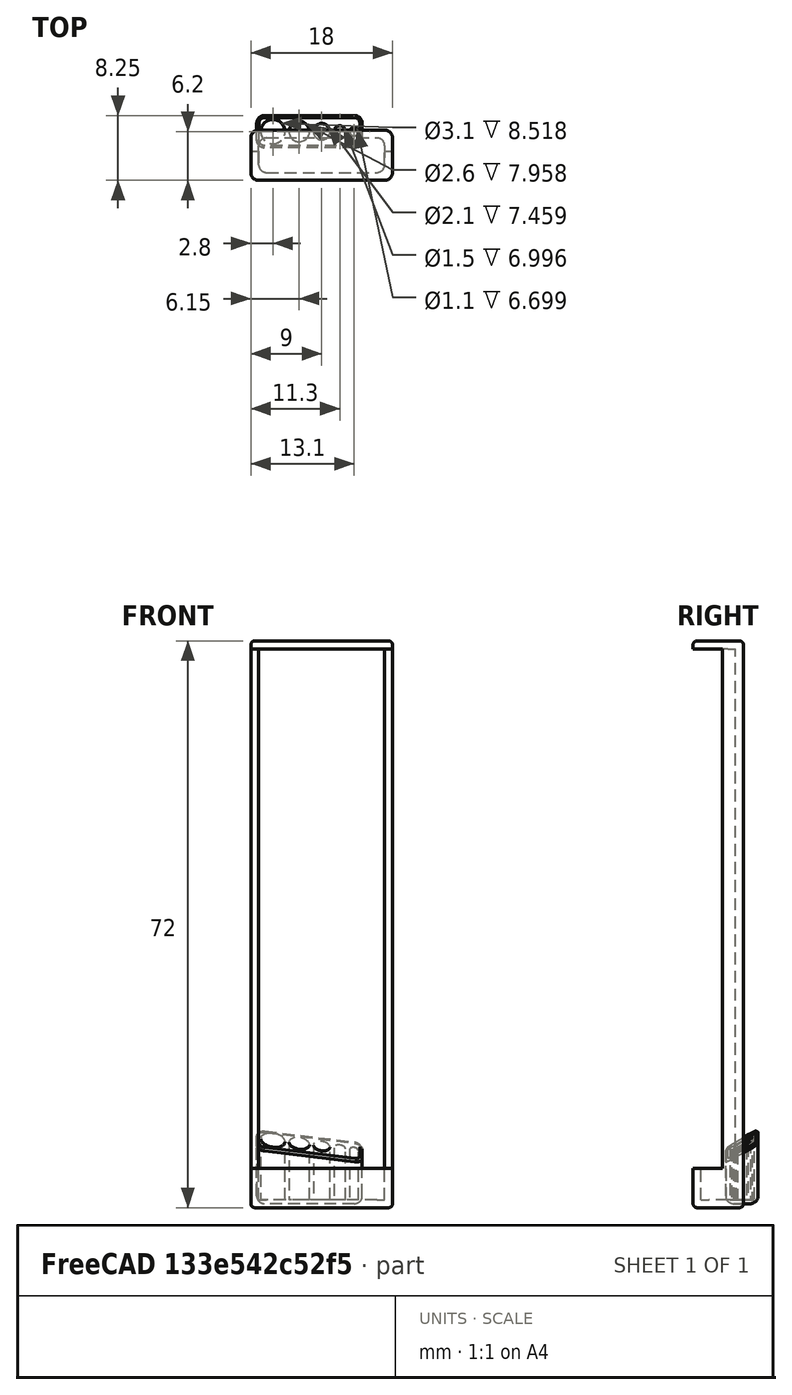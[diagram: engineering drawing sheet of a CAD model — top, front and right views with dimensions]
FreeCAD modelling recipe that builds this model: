
FCSTD DOCUMENT  (FreeCAD 0.20R29177 (Git))
Label: tiny_drillbit_holder
License: All rights reserved
LicenseURL: http://en.wikipedia.org/wiki/All_rights_reserved
objects: PartDesign::Pad×5, TechDraw::DrawViewDimension×5, Sketcher::SketchObject×4, PartDesign::Fillet×3, TechDraw::DrawProjGroupItem×3, PartDesign::ShapeBinder×2, PartDesign::Draft×2, PartDesign::Body×2, PartDesign::Chamfer×1, TechDraw::DrawSVGTemplate×1, TechDraw::DrawProjGroup×1, TechDraw::DrawPage×1, PartDesign::Pocket×1, PartDesign::Plane×1
note: 33 computed .brp shape members not serialized (recipe doc carries the construction recipe); baked Part::Feature solids carry a one-line shape summary decoded from their .brp

FEATURE [Sketcher::SketchObject] Sketch
  Base_Annotations = Drill Hole sizes (all mm) | 1 | 1.5 | 2 | 2.5 | 3
  FullyConstrained = true
  MapMode = 5
  Support = -> [XY_Plane]
  sketch-geometry (22):
    g0: LineSegment StartX=-8.25 StartY=2.05 StartZ=0 EndX=5.15 EndY=2.05 EndZ=0
    g1: LineSegment StartX=5.15 StartY=2.05 StartZ=0 EndX=5.15 EndY=-2.05 EndZ=0
    g2: LineSegment StartX=5.15 StartY=-2.05 StartZ=0 EndX=-8.25 EndY=-2.05 EndZ=0
    g3: LineSegment StartX=-8.25 StartY=-2.05 StartZ=0 EndX=-8.25 EndY=2.05 EndZ=0
    g4: Circle CenterX=-6.2 CenterY=0 CenterZ=0 NormalX=0 NormalY=0 NormalZ=1 AngleXU=0 Radius=1.55
    g5: Circle CenterX=-2.85 CenterY=0 CenterZ=0 NormalX=0 NormalY=0 NormalZ=1 AngleXU=0 Radius=1.3
    g6: Circle CenterX=0 CenterY=0 CenterZ=0 NormalX=0 NormalY=0 NormalZ=1 AngleXU=0 Radius=1.05
    g7: Circle CenterX=2.3 CenterY=0 CenterZ=0 NormalX=0 NormalY=0 NormalZ=1 AngleXU=0 Radius=0.75
    g8: Circle CenterX=4.1 CenterY=0 CenterZ=0 NormalX=0 NormalY=0 NormalZ=1 AngleXU=0 Radius=0.55
    g9: GeomPoint X=-4.15 Y=0 Z=0
    g10: GeomPoint X=-4.65 Y=0 Z=0
    g11: GeomPoint X=-1.55 Y=0 Z=0
    g12: GeomPoint X=-1.05 Y=0 Z=0
    g13: GeomPoint X=1.05 Y=0 Z=0
    g14: GeomPoint X=1.55 Y=0 Z=0
    g15: GeomPoint X=3.05 Y=0 Z=0
    g16: GeomPoint X=3.55 Y=0 Z=0
    g17: GeomPoint X=4.65 Y=0 Z=0
    g18: GeomPoint X=5.15 Y=0 Z=0
    g19: GeomPoint X=-7.75 Y=0 Z=0
    g20: GeomPoint X=-8.25 Y=0 Z=0
    g21: GeomPoint X=-6.2 Y=1.55 Z=0
  constraints (51):
    c: Coincident(g0,g1)
    c: Coincident(g1,g2)
    c: Coincident(g2,g3)
    c: Coincident(g3,g0)
    c: Horizontal(g0)
    c: Horizontal(g2)
    c: Vertical(g1)
    c: PointOnObject(g4,g-1)
    c: Diameter(g4) = 3.1
    c: PointOnObject(g5,g-1)
    c: PointOnObject(g7,g-1)
    c: PointOnObject(g8,g-1)
    c: Diameter(g8) = 1.1
    c: Diameter(g7) = 1.5
    c: Diameter(g6) = 2.1
    c: Diameter(g5) = 2.6
    c: Coincident(g6,g-1)
    c: PointOnObject(g9,g5)
    c: PointOnObject(g10,g4)
    c: PointOnObject(g11,g5)
    c: PointOnObject(g12,g6)
    c: PointOnObject(g13,g6)
    c: PointOnObject(g14,g7)
    c: PointOnObject(g15,g7)
    c: PointOnObject(g16,g8)
    c: PointOnObject(g17,g8)
    c: PointOnObject(g18,g1)
    c: PointOnObject(g19,g4)
    c: PointOnObject(g20,g3)
    c: PointOnObject(g17,g-1)
    c: PointOnObject(g16,g-1)
    c: PointOnObject(g15,g-1)
    c: PointOnObject(g14,g-1)
    c: PointOnObject(g13,g-1)
    c: PointOnObject(g11,g-1)
    c: PointOnObject(g9,g-1)
    c: PointOnObject(g10,g-1)
    c: PointOnObject(g19,g-1)
    c: PointOnObject(g20,g-1)
    c: PointOnObject(g18,g-1)
    c: DistanceX(g15,g16) = 0.5
    c: DistanceX(g13,g14) = 0.5
    c: PointOnObject(g12,g-1)
    c: DistanceX(g11,g12) = 0.5
    c: DistanceX(g20,g19) = 0.5
    c: DistanceX(g10,g9) = 0.5
    c: DistanceX(g17,g18) = 0.5
    c: PointOnObject(g21,g4)
    c: Vertical(g21,g4)
    c: DistanceY(g21,g0) = 0.5
    c: Symmetric(g0,g2,g-1)
FEATURE [PartDesign::ShapeBinder] ShapeBinder
  Support = -> [Sketch]
  TraceSupport = false
FEATURE [PartDesign::Pad] Pad
  Direction = (0,0,1)
  Length = 0.5
  Length2 = 10
  Profile = -> ShapeBinder
  Reversed = true
  Type = 0
FEATURE [PartDesign::Pad] Pad001
  BaseFeature = -> Pad
  Direction = (0,0,1)
  Length = 9
  Length2 = 10
  Profile = -> Sketch
  ReferenceAxis = -> Sketch [N_Axis]
  Type = 0
FEATURE [PartDesign::Draft] Draft
  Angle = 30
  Base = -> Pad001 [Face9]
  BaseFeature = -> Pad001
  SupportTransform = false
FEATURE [PartDesign::Draft] Draft001
  Angle = 6
  Base = -> Draft [Face9]
  BaseFeature = -> Draft
  NeutralPlane = -> Draft [Face8]
  Reversed = true
  SupportTransform = false
FEATURE [PartDesign::Fillet] Fillet
  Base = -> Draft001 [Edge11,Edge1,Edge7,Edge16,Edge5,Edge14,Edge18,Edge8,Edge10,Edge2,Edge12,Edge4]
  BaseFeature = -> Draft001
  Radius = 1
  SupportTransform = false
  UseAllEdges = false
FEATURE [PartDesign::Chamfer] Chamfer
  Angle = 45
  Base = -> Fillet [Edge8,Edge6,Edge5,Edge7,Edge9,Edge11,Edge1,Edge10]
  BaseFeature = -> Fillet
  ChamferType = 0
  FlipDirection = false
  Size = 0.3
  Size2 = 1
  SupportTransform = false
  UseAllEdges = false
FEATURE [PartDesign::Body] Body
  Group = -> [Sketch,ShapeBinder,Pad,Pad001,Draft,Draft001,Fillet,Chamfer]
  Origin = -> Origin
  Placement = pos=(0,3,0) rot=(0,0,1;0rad)
  Tip = -> Chamfer
FEATURE [TechDraw::DrawSVGTemplate] Template
  Height = 210
  Orientation = 1
  Width = 297
FEATURE [TechDraw::DrawProjGroupItem] ProjItem  label="Front"
  CoarseView = false
  Direction = (0,0,-1)
  Focus = 100
  HardHidden = false
  IsoCount = 0
  IsoHidden = false
  IsoVisible = false
  LockPosition = true
  Perspective = false
  Rotation = 0
  RotationVector = (1,0,0)
  Scale = 4
  ScaleType = 2
  SeamHidden = false
  SeamVisible = true
  SmoothHidden = false
  SmoothVisible = true
  Source = -> [Body]
  Type = 0
  X = 0
  XDirection = (1,0,0)
  Y = 0
FEATURE [TechDraw::DrawProjGroupItem] ProjItem001  label="Left"
  CoarseView = false
  Direction = (-1,0,-1e-16)
  Focus = 100
  HardHidden = false
  IsoCount = 0
  IsoHidden = false
  IsoVisible = false
  LockPosition = false
  Perspective = false
  Rotation = 0
  RotationVector = (1,0,0)
  Scale = 4
  ScaleType = 2
  SeamHidden = false
  SeamVisible = true
  SmoothHidden = false
  SmoothVisible = true
  Source = -> [Body]
  Type = 1
  X = 60.2775
  XDirection = (1e-16,0,-1)
  Y = 0
FEATURE [TechDraw::DrawProjGroupItem] ProjItem002  label="Top"
  CoarseView = false
  Direction = (0,-1,0)
  Focus = 100
  HardHidden = false
  IsoCount = 0
  IsoHidden = false
  IsoVisible = false
  LockPosition = false
  Perspective = false
  Rotation = 0
  RotationVector = (1,0,0)
  Scale = 4
  ScaleType = 2
  SeamHidden = false
  SeamVisible = true
  SmoothHidden = false
  SmoothVisible = true
  Source = -> [Body]
  Type = 4
  X = 0
  XDirection = (1,0,0)
  Y = -51.9549
FEATURE [TechDraw::DrawProjGroup] ProjGroup
  Anchor = -> ProjItem
  AutoDistribute = true
  LockPosition = false
  ProjectionType = 0
  Rotation = 0
  Scale = 4
  ScaleType = 2
  Source = -> [Body]
  Views = -> [ProjItem,ProjItem001,ProjItem002]
  X = 117.659
  Y = 133.282
  spacingX = 15
  spacingY = 15
FEATURE [TechDraw::DrawViewDimension] Dimension
  AngleOverride = false
  Arbitrary = false
  ArbitraryTolerances = false
  EqualTolerance = true
  ExtensionAngle = 0
  FormatSpec = %.2f
  FormatSpecOverTolerance = %+.2f
  FormatSpecUnderTolerance = %+.2f
  Inverted = false
  LineAngle = 0
  LockPosition = false
  MeasureType = 1
  OverTolerance = 0
  References2D = -> [ProjItem]
  Rotation = 0
  ScaleType = 0
  TheoreticalExact = false
  Type = 1
  UnderTolerance = 0
  X = 0.767824
  Y = 30.3865
FEATURE [TechDraw::DrawViewDimension] Dimension001
  AngleOverride = false
  Arbitrary = false
  ArbitraryTolerances = false
  EqualTolerance = true
  ExtensionAngle = 0
  FormatSpec = %.2f
  FormatSpecOverTolerance = %+.2f
  FormatSpecUnderTolerance = %+.2f
  Inverted = false
  LineAngle = 0
  LockPosition = false
  MeasureType = 1
  OverTolerance = 0
  References2D = -> [ProjItem]
  Rotation = 0
  ScaleType = 0
  TheoreticalExact = false
  Type = 2
  UnderTolerance = 0
  X = -51.8494
  Y = 2.12797
FEATURE [TechDraw::DrawViewDimension] Dimension002
  AngleOverride = false
  Arbitrary = false
  ArbitraryTolerances = false
  EqualTolerance = true
  ExtensionAngle = 0
  FormatSpec = R%.2f
  FormatSpecOverTolerance = %+.2f
  FormatSpecUnderTolerance = %+.2f
  Inverted = false
  LineAngle = 0
  LockPosition = false
  MeasureType = 1
  OverTolerance = 0
  References2D = -> [ProjItem]
  Rotation = 0
  ScaleType = 0
  TheoreticalExact = false
  Type = 4
  UnderTolerance = 0
  X = -32.5046
  Y = 16.7642
FEATURE [TechDraw::DrawViewDimension] Dimension003
  AngleOverride = false
  Arbitrary = false
  ArbitraryTolerances = false
  EqualTolerance = true
  ExtensionAngle = 0
  FormatSpec = %.2f
  FormatSpecOverTolerance = %+.2f
  FormatSpecUnderTolerance = %+.2f
  Inverted = false
  LineAngle = 0
  LockPosition = false
  MeasureType = 1
  OverTolerance = 0
  References2D = -> [ProjItem002]
  Rotation = 0
  ScaleType = 0
  TheoreticalExact = false
  Type = 2
  UnderTolerance = 0
  X = 37.6446
  Y = -1.60291
FEATURE [TechDraw::DrawViewDimension] Dimension004
  AngleOverride = false
  Arbitrary = false
  ArbitraryTolerances = false
  EqualTolerance = true
  ExtensionAngle = 0
  FormatSpec = R%.2f
  FormatSpecOverTolerance = %+.2f
  FormatSpecUnderTolerance = %+.2f
  Inverted = false
  LineAngle = 0
  LockPosition = false
  MeasureType = 1
  OverTolerance = 0
  References2D = -> [ProjItem002]
  Rotation = 0
  ScaleType = 0
  TheoreticalExact = false
  Type = 4
  UnderTolerance = 0
  X = -34.2962
  Y = -22.1389
FEATURE [TechDraw::DrawPage] Page
  KeepUpdated = true
  NextBalloonIndex = 1
  ProjectionType = 0
  Template = -> Template
  Views = -> [ProjGroup,Dimension,Dimension001,Dimension002,Dimension003,Dimension004]
FEATURE [Sketcher::SketchObject] Sketch001
  FullyConstrained = true
  MapMode = 5
  Support = -> [XY_Plane001]
  sketch-geometry (20):
    g0: ArcOfCircle CenterX=-7 CenterY=1.2 CenterZ=0 NormalX=0 NormalY=0 NormalZ=1 AngleXU=0 Radius=1 StartAngle=1.5708 EndAngle=3.14159
    g1: LineSegment StartX=-7 StartY=2.2 StartZ=0 EndX=7 EndY=2.2 EndZ=0
    g2: ArcOfCircle CenterX=7 CenterY=1.2 CenterZ=0 NormalX=0 NormalY=0 NormalZ=1 AngleXU=0 Radius=1 StartAngle=1e-16 EndAngle=1.5708
    g3: LineSegment StartX=8 StartY=1.2 StartZ=0 EndX=8 EndY=-1.2 EndZ=0
    g4: ArcOfCircle CenterX=7 CenterY=-1.2 CenterZ=0 NormalX=0 NormalY=0 NormalZ=1 AngleXU=0 Radius=1 StartAngle=4.71239 EndAngle=6.28319
    g5: LineSegment StartX=7 StartY=-2.2 StartZ=0 EndX=-7 EndY=-2.2 EndZ=0
    g6: ArcOfCircle CenterX=-7 CenterY=-1.2 CenterZ=0 NormalX=0 NormalY=0 NormalZ=1 AngleXU=0 Radius=1 StartAngle=3.14159 EndAngle=4.71239
    g7: LineSegment StartX=-8 StartY=-1.2 StartZ=0 EndX=-8 EndY=1.2 EndZ=0
    g8: GeomPoint X=-8 Y=2.2 Z=0
    g9: GeomPoint X=8 Y=-2.2 Z=0
    g10: ArcOfCircle CenterX=-8 CenterY=2.2 CenterZ=0 NormalX=0 NormalY=0 NormalZ=1 AngleXU=0 Radius=1 StartAngle=1.5708 EndAngle=3.14159
    g11: LineSegment StartX=-8 StartY=3.2 StartZ=0 EndX=8 EndY=3.2 EndZ=0
    g12: ArcOfCircle CenterX=8 CenterY=2.2 CenterZ=0 NormalX=0 NormalY=0 NormalZ=1 AngleXU=0 Radius=1 StartAngle=2e-16 EndAngle=1.5708
    g13: LineSegment StartX=9 StartY=2.2 StartZ=0 EndX=9 EndY=-2.2 EndZ=0
    g14: ArcOfCircle CenterX=8 CenterY=-2.2 CenterZ=0 NormalX=0 NormalY=0 NormalZ=1 AngleXU=0 Radius=1 StartAngle=4.71239 EndAngle=6.28319
    g15: LineSegment StartX=8 StartY=-3.2 StartZ=0 EndX=-8 EndY=-3.2 EndZ=0
    g16: ArcOfCircle CenterX=-8 CenterY=-2.2 CenterZ=0 NormalX=0 NormalY=0 NormalZ=1 AngleXU=0 Radius=1 StartAngle=3.14159 EndAngle=4.71239
    g17: LineSegment StartX=-9 StartY=-2.2 StartZ=0 EndX=-9 EndY=2.2 EndZ=0
    g18: GeomPoint X=-9 Y=3.2 Z=0
    g19: GeomPoint X=9 Y=-3.2 Z=0
  constraints (46):
    c: Tangent(g0,g1) = 1.5708
    c: Tangent(g1,g2) = 1.5708
    c: Tangent(g2,g3) = 1.5708
    c: Tangent(g3,g4) = 1.5708
    c: Tangent(g4,g5) = 1.5708
    c: Tangent(g5,g6) = 1.5708
    c: Tangent(g6,g7) = 1.5708
    c: Tangent(g7,g0) = 1.5708
    c: Horizontal(g1)
    c: Horizontal(g5)
    c: Vertical(g3)
    c: Vertical(g7)
    c: Equal(g0,g2)
    c: Equal(g2,g4)
    c: Equal(g4,g6)
    c: PointOnObject(g8,g1)
    c: PointOnObject(g8,g7)
    c: PointOnObject(g9,g3)
    c: PointOnObject(g9,g5)
    c: Tangent(g10,g11) = 1.5708
    c: Tangent(g11,g12) = 1.5708
    c: Tangent(g12,g13) = 1.5708
    c: Tangent(g13,g14) = 1.5708
    c: Tangent(g14,g15) = 1.5708
    c: Tangent(g15,g16) = 1.5708
    c: Tangent(g16,g17) = 1.5708
    c: Tangent(g17,g10) = 1.5708
    c: Horizontal(g11)
    c: Horizontal(g15)
    c: Vertical(g13)
    c: Vertical(g17)
    c: Equal(g10,g12)
    c: Equal(g12,g14)
    c: Equal(g14,g16)
    c: PointOnObject(g18,g11)
    c: PointOnObject(g18,g17)
    c: PointOnObject(g19,g13)
    c: PointOnObject(g19,g15)
    c: Symmetric(g4,g0,g-1)
    c: Symmetric(g14,g10,g-1)
    c: DistanceX(g10,g0) = 1
    c: DistanceY(g0,g10) = 1
    c: Radius(g6) = 1
    c: DistanceY(g4,g1) = 4.4
    c: DistanceX(g5,g5) = 14
    c: Equal(g16,g6)
FEATURE [PartDesign::ShapeBinder] ShapeBinder001
  Support = -> [Sketch001]
  TraceSupport = false
FEATURE [PartDesign::Pad] Pad002
  Direction = (0,0,1)
  Length = 1
  Length2 = 10
  Profile = -> ShapeBinder001
  Reversed = true
  Type = 0
FEATURE [PartDesign::Pad] Pad003
  BaseFeature = -> Pad002
  Direction = (0,0,1)
  Length = 70
  Length2 = 10
  Profile = -> Sketch001
  ReferenceAxis = -> Sketch001 [N_Axis]
  Type = 0
FEATURE [Sketcher::SketchObject] Sketch002
  ExternalGeometry = -> [Sketch001]
  FullyConstrained = true
  MapMode = 5
  Placement = pos=(0,0,0) rot=(1,0,0;1.5708rad)
  Support = -> [XZ_Plane001]
  sketch-geometry (4):
    g0: LineSegment StartX=-9 StartY=4 StartZ=0 EndX=9 EndY=4 EndZ=0
    g1: LineSegment StartX=9 StartY=4 StartZ=0 EndX=9 EndY=70 EndZ=0
    g2: LineSegment StartX=9 StartY=70 StartZ=0 EndX=-9 EndY=70 EndZ=0
    g3: LineSegment StartX=-9 StartY=70 StartZ=0 EndX=-9 EndY=4 EndZ=0
  constraints (11):
    c: Coincident(g0,g1)
    c: Coincident(g1,g2)
    c: Coincident(g2,g3)
    c: Coincident(g3,g0)
    c: Horizontal(g2)
    c: Vertical(g1)
    c: Vertical(g3)
    c: Symmetric(g0,g0,g-2)
    c: Vertical(g0,g-3)
    c: DistanceY(g-3,g0) = 4
    c: DistanceY(g-3,g2) = 70
FEATURE [PartDesign::Pocket] Pocket
  BaseFeature = -> Pad003
  Direction = (0,1,-2e-16)
  Length = 5
  Length2 = 0.5
  Profile = -> Sketch002
  ReferenceAxis = -> Sketch002 [N_Axis]
  Reversed = true
  Type = 4
FEATURE [PartDesign::Plane] DatumPlane
  AttachmentOffset = pos=(0,0,70) rot=(0,0,1;0rad)
  Length = 60
  MapMode = 5
  Placement = pos=(0,0,70) rot=(0,0,1;0rad)
  ResizeMode = 0
  Support = -> [XY_Plane001]
  Width = 60
FEATURE [Sketcher::SketchObject] Sketch003
  ExternalGeometry = -> [Sketch001]
  FullyConstrained = true
  MapMode = 5
  Placement = pos=(0,0,70) rot=(0,0,1;0rad)
  Support = -> [DatumPlane]
  sketch-geometry (10):
    g0: ArcOfCircle CenterX=-8 CenterY=2.2 CenterZ=0 NormalX=0 NormalY=0 NormalZ=1 AngleXU=0 Radius=1 StartAngle=1.5708 EndAngle=3.14159
    g1: LineSegment StartX=-8 StartY=3.2 StartZ=0 EndX=8 EndY=3.2 EndZ=0
    g2: ArcOfCircle CenterX=8 CenterY=2.2 CenterZ=0 NormalX=0 NormalY=0 NormalZ=1 AngleXU=0 Radius=1 StartAngle=1e-16 EndAngle=1.5708
    g3: LineSegment StartX=9 StartY=2.2 StartZ=0 EndX=9 EndY=-2.2 EndZ=0
    g4: ArcOfCircle CenterX=8 CenterY=-2.2 CenterZ=0 NormalX=0 NormalY=0 NormalZ=1 AngleXU=0 Radius=1 StartAngle=4.71239 EndAngle=6.28319
    g5: LineSegment StartX=8 StartY=-3.2 StartZ=0 EndX=-8 EndY=-3.2 EndZ=0
    g6: ArcOfCircle CenterX=-8 CenterY=-2.2 CenterZ=0 NormalX=0 NormalY=0 NormalZ=1 AngleXU=0 Radius=1 StartAngle=3.14159 EndAngle=4.71239
    g7: LineSegment StartX=-9 StartY=-2.2 StartZ=0 EndX=-9 EndY=2.2 EndZ=0
    g8: GeomPoint X=-9 Y=3.2 Z=0
    g9: GeomPoint X=9 Y=-3.2 Z=0
  constraints (22):
    c: Tangent(g0,g1) = 1.5708
    c: Tangent(g1,g2) = 1.5708
    c: Tangent(g2,g3) = 1.5708
    c: Tangent(g3,g4) = 1.5708
    c: Tangent(g4,g5) = 1.5708
    c: Tangent(g5,g6) = 1.5708
    c: Tangent(g6,g7) = 1.5708
    c: Tangent(g7,g0) = 1.5708
    c: Horizontal(g5)
    c: Vertical(g3)
    c: Vertical(g7)
    c: Equal(g0,g2)
    c: Equal(g2,g4)
    c: Equal(g4,g6)
    c: PointOnObject(g8,g1)
    c: PointOnObject(g8,g7)
    c: PointOnObject(g9,g3)
    c: PointOnObject(g9,g5)
    c: Symmetric(g0,g4,g-1)
    c: Tangent(g1,g-4)
    c: Equal(g-5,g2)
    c: Equal(g1,g-4)
FEATURE [PartDesign::Pad] Pad004
  BaseFeature = -> Pocket
  Direction = (0,0,1)
  Length = 1
  Length2 = 10
  Profile = -> Sketch003
  ReferenceAxis = -> Sketch003 [N_Axis]
  Type = 0
FEATURE [PartDesign::Fillet] Fillet001
  Base = -> Pad004 [Edge96,Edge95,Edge76,Edge92,Edge91,Edge89,Edge72,Edge94]
  BaseFeature = -> Pad004
  Radius = 0.5
  SupportTransform = false
  UseAllEdges = false
FEATURE [PartDesign::Fillet] Fillet002
  Base = -> Fillet001 [Edge93,Edge97,Edge96,Edge95,Edge94,Edge85,Edge46,Edge92]
  BaseFeature = -> Fillet001
  Radius = 0.5
  SupportTransform = false
  UseAllEdges = false
FEATURE [PartDesign::Body] Body001  label="DrillbitTray"
  Group = -> [Sketch001,ShapeBinder001,Pad002,Pad003,Sketch002,Pocket,DatumPlane,Sketch003,Pad004,Fillet001,Fillet002]
  Origin = -> Origin001
  Tip = -> Fillet002
